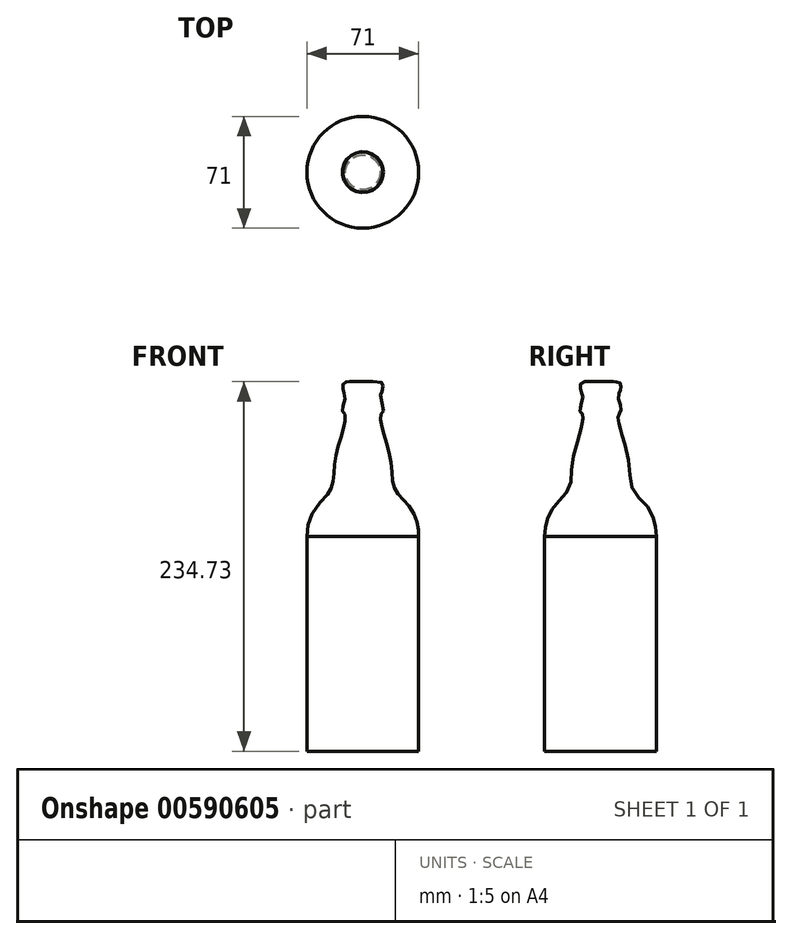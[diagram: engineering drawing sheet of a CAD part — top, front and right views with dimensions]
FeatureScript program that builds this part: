
annotation { "Feature Type Name" : "Feature", "Feature Type Description" : "" }
export const myFeature = defineFeature(function(context is Context, id is Id, definition is map)
    precondition{}
    {
        {
            var Q0;
            Q0=qCreatedBy(makeId("Front.planeOp"),FACE);
            var sketch = newSketch(context, id + "F0", { "sketchPlane" : qUnion([Q0])});
            skPoint(sketch, "E0", {"position": v(0, 0) * mm});
            skLineSegment(sketch, "E1", {"start": v(0, 0) * mm, "end": v(35.5, 0) * mm});
            skLineSegment(sketch, "E2", {"start": v(35.5, 136.36) * mm, "end": v(35.5, 0) * mm});
            skPoint(sketch, "E3.9.internal.snap0", {"position": v(0, 234.71) * mm});
            skLineSegment(sketch, "E4", {"start": v(0, 234.71) * mm, "end": v(0, 0) * mm});
            skFitSpline(sketch, "E5", {"points": [v(35.5, 136.36) * mm, v(34.62, 144.32) * mm, v(29.52, 155.44) * mm, v(22.31, 163.18) * mm, v(19, 170.57) * mm, v(17.93, 183.34) * mm, v(14.32, 198.24) * mm, v(11.73, 207.82) * mm, v(11.39, 213.96) * mm, v(12.94, 215.7) * mm, v(11.18, 225.92) * mm, v(12.18, 228.1) * mm, v(12.72, 232.85) * mm, v(0, 234.71) * mm], "startDerivative": vector(-3.61, 93.13) * mm, "endDerivative": vector(-362, 0) * mm});
            skSolve(sketch);
        }
        {
            var Q0;
            Q0=makeQuery(id+"F0.imprint","IMPRINT",FACE,{"disambiguationData":[TD([[makeQuery(id+"F0.imprint","IMPRINT",EDGE,{"derivedFrom":sQuery(id+"F0.wireOp",EDGE,"E1")}),1.0]])]});
            var Q1;
            Q1=sQuery(id+"F0.wireOp",EDGE,"E4");
            revolve(context, id + "F1", {"entities" : qUnion([Q0]), "axis" : qUnion([Q1]), "revolveType" : RevolveType.FULL});
        }
    });
